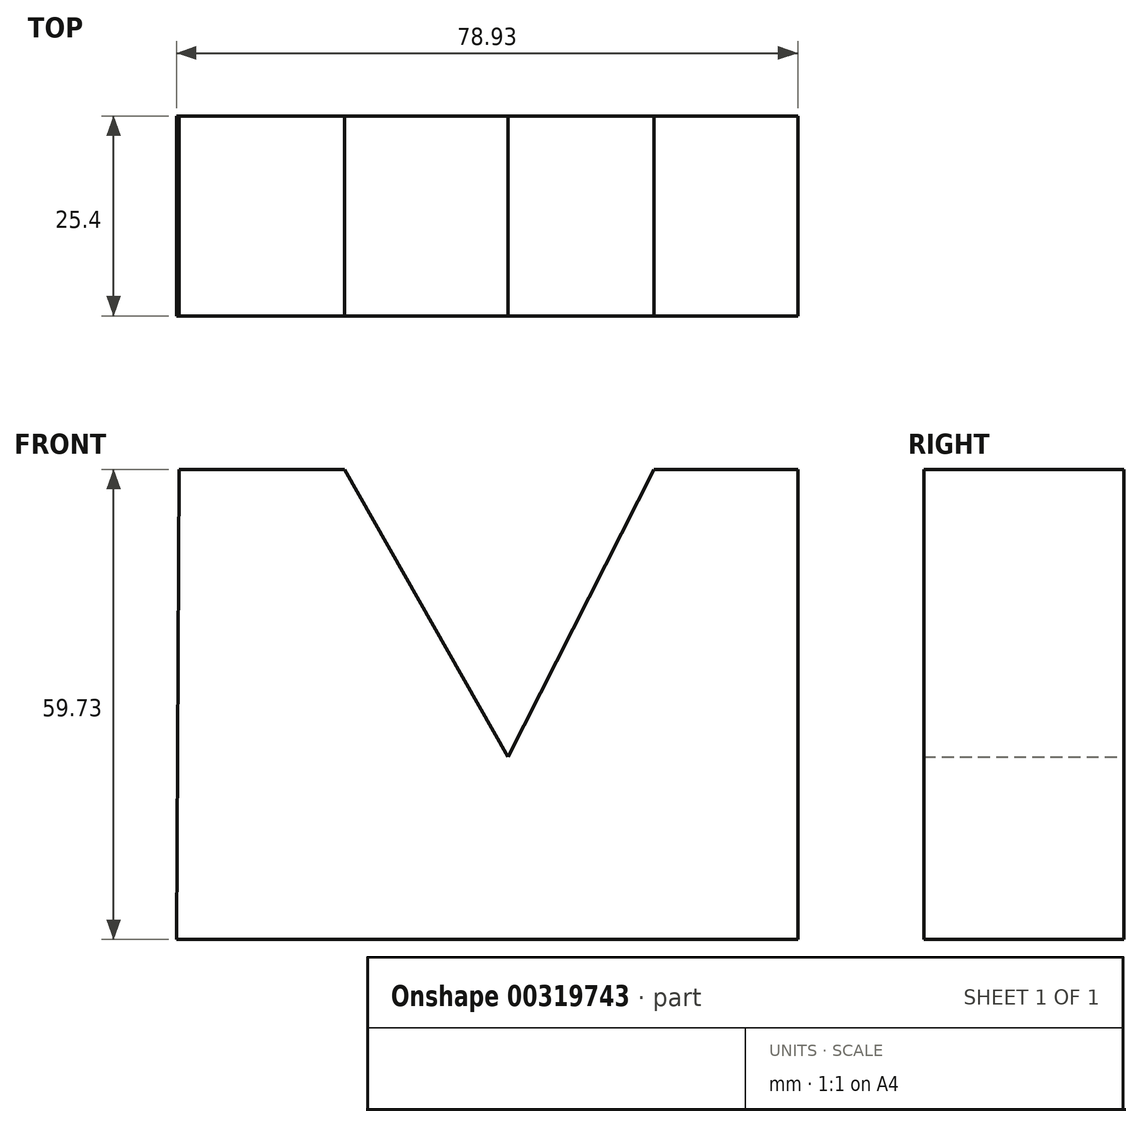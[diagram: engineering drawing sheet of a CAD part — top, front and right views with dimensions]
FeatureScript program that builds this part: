
annotation { "Feature Type Name" : "Feature", "Feature Type Description" : "" }
export const myFeature = defineFeature(function(context is Context, id is Id, definition is map)
    precondition{}
    {
        {
            var Q0;
            Q0=qCreatedBy(makeId("Front.planeOp"),FACE);
            var sketch = newSketch(context, id + "F0", { "sketchPlane" : qUnion([Q0])});
            skLineSegment(sketch, "E0", {"start": v(-50.76, 40.4) * mm, "end": v(-29.71, 40.4) * mm});
            skLineSegment(sketch, "E1", {"start": v(-29.71, 40.4) * mm, "end": v(-8.98, 3.87) * mm});
            skLineSegment(sketch, "E2", {"start": v(-8.98, 3.87) * mm, "end": v(9.6, 40.4) * mm});
            skLineSegment(sketch, "E3", {"start": v(9.6, 40.4) * mm, "end": v(27.86, 40.4) * mm});
            skLineSegment(sketch, "E4", {"start": v(27.86, 40.4) * mm, "end": v(27.86, -19.34) * mm});
            skLineSegment(sketch, "E5", {"start": v(27.86, -19.34) * mm, "end": v(-51.07, -19.34) * mm});
            skLineSegment(sketch, "E6", {"start": v(-51.07, -19.34) * mm, "end": v(-50.76, 40.4) * mm});
            skSolve(sketch);
        }
        {
            var Q0;
            Q0=makeQuery(id+"F0.imprint","IMPRINT",FACE,{"disambiguationData":[TD([[makeQuery(id+"F0.imprint","IMPRINT",EDGE,{"derivedFrom":sQuery(id+"F0.wireOp",EDGE,"E0")}),-1.0]])]});
            extrude(context, id + "F1", {"entities" : qUnion([Q0]), "depth" : 25.4 * mm});
        }
    });
